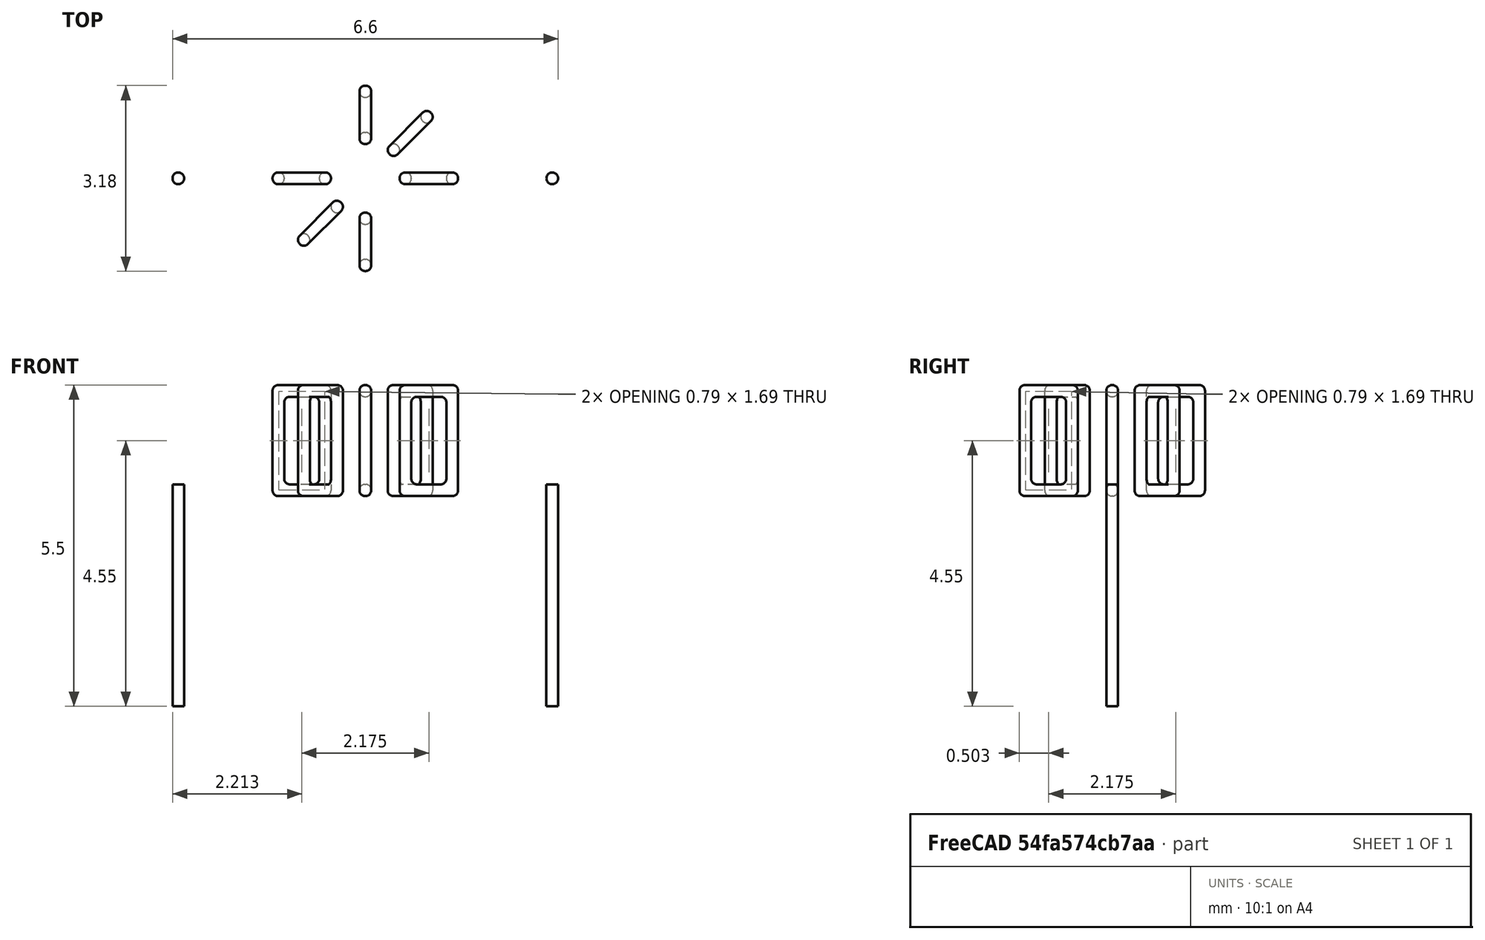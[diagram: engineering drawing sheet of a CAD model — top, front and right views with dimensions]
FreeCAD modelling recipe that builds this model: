
FCSTD DOCUMENT  (FreeCAD 0.16R6703 (Git))
Label: L_Toroid_Horizontal_D3.2mm_P6.40mm_Diameter3-5mm_Amidon-T12
License: All rights reserved
LicenseURL: http://en.wikipedia.org/wiki/All_rights_reserved
objects: Sketcher::SketchObject×6, PartDesign::Pad×6, PartDesign::Fillet×5, Spreadsheet::Sheet×1
note: 23 computed .brp shape members not serialized (recipe doc carries the construction recipe); baked Part::Feature solids carry a one-line shape summary decoded from their .brp

FEATURE [Spreadsheet::Sheet] Spreadsheet  label="dimensions"
  cells = A1=Wx; B1(Wx)=3.175; C1(WW)=1.5748; D1=3.175; A2=Wy; B2(Wy)=3.175; D2=3.175; A3=RM; B3(RMx)=6.4; C3(RMy)=0; A4=d_wire; B4(d_wire)=0.2; A5=H; B5(H)=1.5; A6=offsetx; B6(offsetx)=-1.6125
FEATURE [Sketcher::SketchObject] Sketch
  Placement = pos=(0,0,0.7) rot=(0,0,1;0rad)
  expr: Placement.Base.z = 0.5 + Spreadsheet.d_wire
  expr: Constraints[0] = Spreadsheet.Wx / 2 - Spreadsheet.d_wire
  expr: Constraints[4] = Spreadsheet.WW / 2
  expr: Constraints[2] = Spreadsheet.RMy / 2
  expr: Constraints[1] = Spreadsheet.RMx / 2
  sketch-geometry (2):
    g0: Circle CenterX=3.2 CenterY=0 CenterZ=0 NormalX=0 NormalY=0 NormalZ=1 Radius=1.3875
    g1: Circle CenterX=3.2 CenterY=0 CenterZ=0 NormalX=0 NormalY=0 NormalZ=1 Radius=0.7874
  constraints (5):
    c: Radius(g0) = 1.3875
    c: DistanceX(g-1,g0) = 3.2
    c: DistanceY(g-1,g0) = 0
    c: Coincident(g1,g0)
    c: Radius(g1) = 0.7874
FEATURE [PartDesign::Pad] Pad
  Length = 1.5
  Length2 = 100
  Placement = pos=(0,0,0.7) rot=(0,0,1;0rad)
  Sketch = -> Sketch
  Type = 0
  expr: Length = Spreadsheet.H
FEATURE [Sketcher::SketchObject] Sketch001
  Placement = pos=(0,0,0.6) rot=(0,0,1;0rad)
  expr: Placement.Base.z = 0.5 + Spreadsheet.d_wire * 0.5
  expr: Constraints[4] = Spreadsheet.RMx
  expr: Constraints[2] = Spreadsheet.RMy
  expr: Constraints[1] = Spreadsheet.d_wire / 2
  sketch-geometry (2):
    g0: Circle CenterX=0 CenterY=0 CenterZ=0 NormalX=0 NormalY=0 NormalZ=1 Radius=0.1
    g1: Circle CenterX=6.4 CenterY=0 CenterZ=0 NormalX=0 NormalY=0 NormalZ=1 Radius=0.1
  constraints (5):
    c: Equal(g0,g1)
    c: Radius(g0) = 0.1
    c: DistanceY(g-1,g1) = 0
    c: Coincident(g0,g-1)
    c: DistanceX(g-1,g1) = 6.4
FEATURE [PartDesign::Pad] Pad001
  Length = 0.1
  Length2 = 3.7
  Placement = pos=(0,0,0.6) rot=(0,0,1;0rad)
  Reversed = true
  Sketch = -> Sketch001
  Type = 4
  expr: Length2 = 3.5 + Spreadsheet.d_wire
  expr: Length = Spreadsheet.d_wire / 2
FEATURE [PartDesign::Fillet] Fillet
  Base = -> Pad [Edge6,Edge3,Edge2]
  Placement = pos=(0,0,0.7) rot=(0,0,1;0rad)
  Radius = 0.5
FEATURE [Sketcher::SketchObject] Sketch003
  Placement = pos=(3.2,0,0) rot=(1,0,0;1.5708rad)
  expr: Placement.Base.x = Spreadsheet.RMx / 2
  expr: Constraints[49] = Spreadsheet.Wx - Spreadsheet.d_wire * 2
  expr: Constraints[44] = Spreadsheet.d_wire
  expr: Constraints[23] = Spreadsheet.H
  expr: Constraints[22] = Spreadsheet.Wx / 2 - Spreadsheet.d_wire
  expr: Placement.Base.y = Spreadsheet.RMy / 2
  expr: Constraints[21] = (Spreadsheet.Wx - Spreadsheet.WW) / 2 - Spreadsheet.d_wire
  expr: Constraints[19] = Spreadsheet.d_wire
  expr: Constraints[17] = Spreadsheet.d_wire
  expr: Constraints[18] = Spreadsheet.d_wire
  expr: Constraints[16] = Spreadsheet.d_wire
  sketch-geometry (16):
    g0: LineSegment StartX=-0.5874 StartY=0.5 StartZ=0 EndX=-1.5875 EndY=0.5 EndZ=0
    g1: LineSegment StartX=-1.5875 StartY=0.5 StartZ=0 EndX=-1.5875 EndY=2.4 EndZ=0
    g2: LineSegment StartX=-1.5875 StartY=2.4 StartZ=0 EndX=-0.5874 EndY=2.4 EndZ=0
    g3: LineSegment StartX=-0.5874 StartY=2.4 StartZ=0 EndX=-0.5874 EndY=0.5 EndZ=0
    g4: LineSegment StartX=-1.3875 StartY=2.2 StartZ=0 EndX=-0.7874 EndY=2.2 EndZ=0
    g5: LineSegment StartX=-0.7874 StartY=2.2 StartZ=0 EndX=-0.7874 EndY=0.7 EndZ=0
    g6: LineSegment StartX=-0.7874 StartY=0.7 StartZ=0 EndX=-1.3875 EndY=0.7 EndZ=0
    g7: LineSegment StartX=-1.3875 StartY=0.7 StartZ=0 EndX=-1.3875 EndY=2.2 EndZ=0
    g8: LineSegment StartX=0.5874 StartY=2.4 StartZ=0 EndX=1.5875 EndY=2.4 EndZ=0
    g9: LineSegment StartX=1.5875 StartY=2.4 StartZ=0 EndX=1.5875 EndY=0.5 EndZ=0
    g10: LineSegment StartX=1.5875 StartY=0.5 StartZ=0 EndX=0.5874 EndY=0.5 EndZ=0
    g11: LineSegment StartX=0.5874 StartY=0.5 StartZ=0 EndX=0.5874 EndY=2.4 EndZ=0
    g12: LineSegment StartX=0.7874 StartY=2.2 StartZ=0 EndX=1.3875 EndY=2.2 EndZ=0
    g13: LineSegment StartX=1.3875 StartY=2.2 StartZ=0 EndX=1.3875 EndY=0.7 EndZ=0
    g14: LineSegment StartX=1.3875 StartY=0.7 StartZ=0 EndX=0.7874 EndY=0.7 EndZ=0
    g15: LineSegment StartX=0.7874 StartY=0.7 StartZ=0 EndX=0.7874 EndY=2.2 EndZ=0
  constraints (50):
    c: Horizontal(g0)
    c: Coincident(g1,g0)
    c: Vertical(g1)
    c: Coincident(g2,g1)
    c: Horizontal(g2)
    c: Coincident(g3,g2)
    c: Coincident(g3,g0)
    c: Vertical(g3)
    c: Coincident(g4,g5)
    c: Coincident(g5,g6)
    c: Coincident(g6,g7)
    c: Coincident(g7,g4)
    c: Horizontal(g4)
    c: Horizontal(g6)
    c: Vertical(g5)
    c: Vertical(g7)
    c: DistanceX(g1,g4) = 0.2
    c: DistanceY(g4,g1) = 0.2
    c: DistanceX(g5,g0) = 0.2
    c: DistanceY(g0,g5) = 0.2
    c: DistanceY(g-1,g0) = 0.5
    c: DistanceX(g6,g6) = 0.6001
    c: DistanceX(g6,g-1) = 1.3875
    c: DistanceY(g7,g7) = 1.5
    c: Coincident(g8,g9)
    c: Coincident(g9,g10)
    c: Coincident(g10,g11)
    c: Coincident(g11,g8)
    c: Horizontal(g8)
    c: Horizontal(g10)
    c: Vertical(g9)
    c: Vertical(g11)
    c: Coincident(g12,g13)
    c: Coincident(g13,g14)
    c: Coincident(g14,g15)
    c: Coincident(g15,g12)
    c: Horizontal(g12)
    c: Horizontal(g14)
    c: Vertical(g13)
    c: Vertical(g15)
    c: DistanceY(g8,g2) = 0
    c: DistanceY(g10,g0) = 0
    c: DistanceY(g14,g5) = 0
    c: DistanceY(g12,g4) = 0
    c: DistanceX(g8,g12) = 0.2
    c: Equal(g8,g2)
    c: Equal(g12,g4)
    c: Equal(g9,g1)
    c: Equal(g13,g7)
    c: DistanceX(g4,g12) = 2.775
FEATURE [PartDesign::Pad] Pad002
  Length = 0.2
  Length2 = 100
  Midplane = true
  Placement = pos=(3.2,0,0) rot=(1,0,0;1.5708rad)
  Sketch = -> Sketch003
  Type = 0
  expr: Length = Spreadsheet.d_wire
FEATURE [PartDesign::Fillet] Fillet001
  Base = -> Pad002 [Edge38,Edge41,Edge42,Edge43,Edge29,Edge32,Edge33,Edge34,Edge25,Edge35,Edge36,Edge13,Edge14,Edge15,Edge16,Edge17,Edge18,Edge19,Edge1,Edge2,Edge3,Edge4,Edge5,Edge6,Edge7,Edge37,Edge39,Edge40,Edge20,Edge23,Edge24,Edge21,Edge22,Edge8,Edge9,Edge10,Edge11,Edge12,Edge26,Edge27,+8 more]
  Placement = pos=(3.2,0,0) rot=(1,0,0;1.5708rad)
  Radius = 0.094
  expr: Radius = Spreadsheet.d_wire * 0.47
FEATURE [Sketcher::SketchObject] Sketch004
  Placement = pos=(3.2,0,0) rot=(0.862856,0.357407,0.357407;1.71777rad)
  expr: Placement.Base.x = Spreadsheet.RMx / 2
  expr: Constraints[49] = Spreadsheet.Wx - 2 * Spreadsheet.d_wire
  expr: Constraints[44] = Spreadsheet.d_wire
  expr: Constraints[23] = Spreadsheet.H
  expr: Constraints[22] = Spreadsheet.Wx / 2 - Spreadsheet.d_wire
  expr: Placement.Base.y = Spreadsheet.RMy / 2
  expr: Constraints[21] = (Spreadsheet.Wx - Spreadsheet.WW) / 2 - Spreadsheet.d_wire
  expr: Constraints[19] = Spreadsheet.d_wire
  expr: Constraints[17] = Spreadsheet.d_wire
  expr: Constraints[18] = Spreadsheet.d_wire
  expr: Constraints[16] = Spreadsheet.d_wire
  sketch-geometry (16):
    g0: LineSegment StartX=-0.5874 StartY=0.5 StartZ=0 EndX=-1.5875 EndY=0.5 EndZ=0
    g1: LineSegment StartX=-1.5875 StartY=0.5 StartZ=0 EndX=-1.5875 EndY=2.4 EndZ=0
    g2: LineSegment StartX=-1.5875 StartY=2.4 StartZ=0 EndX=-0.5874 EndY=2.4 EndZ=0
    g3: LineSegment StartX=-0.5874 StartY=2.4 StartZ=0 EndX=-0.5874 EndY=0.5 EndZ=0
    g4: LineSegment StartX=-1.3875 StartY=2.2 StartZ=0 EndX=-0.7874 EndY=2.2 EndZ=0
    g5: LineSegment StartX=-0.7874 StartY=2.2 StartZ=0 EndX=-0.7874 EndY=0.7 EndZ=0
    g6: LineSegment StartX=-0.7874 StartY=0.7 StartZ=0 EndX=-1.3875 EndY=0.7 EndZ=0
    g7: LineSegment StartX=-1.3875 StartY=0.7 StartZ=0 EndX=-1.3875 EndY=2.2 EndZ=0
    g8: LineSegment StartX=0.5874 StartY=2.4 StartZ=0 EndX=1.5875 EndY=2.4 EndZ=0
    g9: LineSegment StartX=1.5875 StartY=2.4 StartZ=0 EndX=1.5875 EndY=0.5 EndZ=0
    g10: LineSegment StartX=1.5875 StartY=0.5 StartZ=0 EndX=0.5874 EndY=0.5 EndZ=0
    g11: LineSegment StartX=0.5874 StartY=0.5 StartZ=0 EndX=0.5874 EndY=2.4 EndZ=0
    g12: LineSegment StartX=0.7874 StartY=2.2 StartZ=0 EndX=1.3875 EndY=2.2 EndZ=0
    g13: LineSegment StartX=1.3875 StartY=2.2 StartZ=0 EndX=1.3875 EndY=0.7 EndZ=0
    g14: LineSegment StartX=1.3875 StartY=0.7 StartZ=0 EndX=0.7874 EndY=0.7 EndZ=0
    g15: LineSegment StartX=0.7874 StartY=0.7 StartZ=0 EndX=0.7874 EndY=2.2 EndZ=0
  constraints (50):
    c: Horizontal(g0)
    c: Coincident(g1,g0)
    c: Vertical(g1)
    c: Coincident(g2,g1)
    c: Horizontal(g2)
    c: Coincident(g3,g2)
    c: Coincident(g3,g0)
    c: Vertical(g3)
    c: Coincident(g4,g5)
    c: Coincident(g5,g6)
    c: Coincident(g6,g7)
    c: Coincident(g7,g4)
    c: Horizontal(g4)
    c: Horizontal(g6)
    c: Vertical(g5)
    c: Vertical(g7)
    c: DistanceX(g1,g4) = 0.2
    c: DistanceY(g4,g1) = 0.2
    c: DistanceX(g5,g0) = 0.2
    c: DistanceY(g0,g5) = 0.2
    c: DistanceY(g-1,g0) = 0.5
    c: DistanceX(g6,g6) = 0.6001
    c: DistanceX(g6,g-1) = 1.3875
    c: DistanceY(g7,g7) = 1.5
    c: Coincident(g8,g9)
    c: Coincident(g9,g10)
    c: Coincident(g10,g11)
    c: Coincident(g11,g8)
    c: Horizontal(g8)
    c: Horizontal(g10)
    c: Vertical(g9)
    c: Vertical(g11)
    c: Coincident(g12,g13)
    c: Coincident(g13,g14)
    c: Coincident(g14,g15)
    c: Coincident(g15,g12)
    c: Horizontal(g12)
    c: Horizontal(g14)
    c: Vertical(g13)
    c: Vertical(g15)
    c: DistanceY(g8,g2) = 0
    c: DistanceY(g10,g0) = 0
    c: DistanceY(g14,g5) = 0
    c: DistanceY(g12,g4) = 0
    c: DistanceX(g8,g12) = 0.2
    c: Equal(g8,g2)
    c: Equal(g12,g4)
    c: Equal(g9,g1)
    c: Equal(g13,g7)
    c: DistanceX(g4,g12) = 2.775
FEATURE [PartDesign::Pad] Pad003
  Length = 0.2
  Length2 = 100
  Midplane = true
  Placement = pos=(3.2,0,0) rot=(0.862856,0.357407,0.357407;1.71777rad)
  Sketch = -> Sketch004
  Type = 0
  expr: Length = Spreadsheet.d_wire
FEATURE [PartDesign::Fillet] Fillet002
  Base = -> Pad003 [Edge38,Edge41,Edge42,Edge43,Edge29,Edge32,Edge33,Edge34,Edge25,Edge35,Edge36,Edge13,Edge14,Edge15,Edge16,Edge17,Edge18,Edge19,Edge1,Edge2,Edge3,Edge4,Edge5,Edge6,Edge7,Edge37,Edge39,Edge40,Edge20,Edge23,Edge24,Edge21,Edge22,Edge8,Edge9,Edge10,Edge11,Edge12,Edge26,Edge27,+8 more]
  Placement = pos=(3.2,0,0) rot=(0.862856,0.357407,0.357407;1.71777rad)
  Radius = 0.094
  expr: Radius = Spreadsheet.d_wire * 0.47
FEATURE [Sketcher::SketchObject] Sketch005
  Placement = pos=(3.2,0,0) rot=(0.862856,-0.357407,-0.357407;1.71777rad)
  expr: Placement.Base.x = Spreadsheet.RMx / 2
  expr: Constraints[49] = Spreadsheet.Wx - 2 * Spreadsheet.d_wire
  expr: Constraints[44] = Spreadsheet.d_wire
  expr: Constraints[23] = Spreadsheet.H
  expr: Constraints[22] = Spreadsheet.Wx / 2 - Spreadsheet.d_wire
  expr: Placement.Base.y = Spreadsheet.RMy / 2
  expr: Constraints[21] = (Spreadsheet.Wx - Spreadsheet.WW) / 2 - Spreadsheet.d_wire
  expr: Constraints[19] = Spreadsheet.d_wire
  expr: Constraints[17] = Spreadsheet.d_wire
  expr: Constraints[18] = Spreadsheet.d_wire
  expr: Constraints[16] = Spreadsheet.d_wire
  sketch-geometry (16):
    g0: LineSegment StartX=-0.5874 StartY=0.5 StartZ=0 EndX=-1.5875 EndY=0.5 EndZ=0
    g1: LineSegment StartX=-1.5875 StartY=0.5 StartZ=0 EndX=-1.5875 EndY=2.4 EndZ=0
    g2: LineSegment StartX=-1.5875 StartY=2.4 StartZ=0 EndX=-0.5874 EndY=2.4 EndZ=0
    g3: LineSegment StartX=-0.5874 StartY=2.4 StartZ=0 EndX=-0.5874 EndY=0.5 EndZ=0
    g4: LineSegment StartX=-1.3875 StartY=2.2 StartZ=0 EndX=-0.7874 EndY=2.2 EndZ=0
    g5: LineSegment StartX=-0.7874 StartY=2.2 StartZ=0 EndX=-0.7874 EndY=0.7 EndZ=0
    g6: LineSegment StartX=-0.7874 StartY=0.7 StartZ=0 EndX=-1.3875 EndY=0.7 EndZ=0
    g7: LineSegment StartX=-1.3875 StartY=0.7 StartZ=0 EndX=-1.3875 EndY=2.2 EndZ=0
    g8: LineSegment StartX=0.5874 StartY=2.4 StartZ=0 EndX=1.5875 EndY=2.4 EndZ=0
    g9: LineSegment StartX=1.5875 StartY=2.4 StartZ=0 EndX=1.5875 EndY=0.5 EndZ=0
    g10: LineSegment StartX=1.5875 StartY=0.5 StartZ=0 EndX=0.5874 EndY=0.5 EndZ=0
    g11: LineSegment StartX=0.5874 StartY=0.5 StartZ=0 EndX=0.5874 EndY=2.4 EndZ=0
    g12: LineSegment StartX=0.7874 StartY=2.2 StartZ=0 EndX=1.3875 EndY=2.2 EndZ=0
    g13: LineSegment StartX=1.3875 StartY=2.2 StartZ=0 EndX=1.3875 EndY=0.7 EndZ=0
    g14: LineSegment StartX=1.3875 StartY=0.7 StartZ=0 EndX=0.7874 EndY=0.7 EndZ=0
    g15: LineSegment StartX=0.7874 StartY=0.7 StartZ=0 EndX=0.7874 EndY=2.2 EndZ=0
  constraints (50):
    c: Horizontal(g0)
    c: Coincident(g1,g0)
    c: Vertical(g1)
    c: Coincident(g2,g1)
    c: Horizontal(g2)
    c: Coincident(g3,g2)
    c: Coincident(g3,g0)
    c: Vertical(g3)
    c: Coincident(g4,g5)
    c: Coincident(g5,g6)
    c: Coincident(g6,g7)
    c: Coincident(g7,g4)
    c: Horizontal(g4)
    c: Horizontal(g6)
    c: Vertical(g5)
    c: Vertical(g7)
    c: DistanceX(g1,g4) = 0.2
    c: DistanceY(g4,g1) = 0.2
    c: DistanceX(g5,g0) = 0.2
    c: DistanceY(g0,g5) = 0.2
    c: DistanceY(g-1,g0) = 0.5
    c: DistanceX(g6,g6) = 0.6001
    c: DistanceX(g6,g-1) = 1.3875
    c: DistanceY(g7,g7) = 1.5
    c: Coincident(g8,g9)
    c: Coincident(g9,g10)
    c: Coincident(g10,g11)
    c: Coincident(g11,g8)
    c: Horizontal(g8)
    c: Horizontal(g10)
    c: Vertical(g9)
    c: Vertical(g11)
    c: Coincident(g12,g13)
    c: Coincident(g13,g14)
    c: Coincident(g14,g15)
    c: Coincident(g15,g12)
    c: Horizontal(g12)
    c: Horizontal(g14)
    c: Vertical(g13)
    c: Vertical(g15)
    c: DistanceY(g8,g2) = 0
    c: DistanceY(g10,g0) = 0
    c: DistanceY(g14,g5) = 0
    c: DistanceY(g12,g4) = 0
    c: DistanceX(g8,g12) = 0.2
    c: Equal(g8,g2)
    c: Equal(g12,g4)
    c: Equal(g9,g1)
    c: Equal(g13,g7)
    c: DistanceX(g4,g12) = 2.775
FEATURE [PartDesign::Pad] Pad004
  Length = 0.2
  Length2 = 100
  Midplane = true
  Placement = pos=(3.2,0,0) rot=(0.862856,-0.357407,-0.357407;1.71777rad)
  Sketch = -> Sketch005
  Type = 0
  expr: Length = Spreadsheet.d_wire
FEATURE [PartDesign::Fillet] Fillet003
  Base = -> Pad004 [Edge38,Edge41,Edge42,Edge43,Edge29,Edge32,Edge33,Edge34,Edge25,Edge35,Edge36,Edge13,Edge14,Edge15,Edge16,Edge17,Edge18,Edge19,Edge1,Edge2,Edge3,Edge4,Edge5,Edge6,Edge7,Edge37,Edge39,Edge40,Edge20,Edge23,Edge24,Edge21,Edge22,Edge8,Edge9,Edge10,Edge11,Edge12,Edge26,Edge27,+8 more]
  Placement = pos=(3.2,0,0) rot=(0.862856,-0.357407,-0.357407;1.71777rad)
  Radius = 0.094
  expr: Radius = Spreadsheet.d_wire * 0.47
FEATURE [Sketcher::SketchObject] Sketch006
  Placement = pos=(3.2,0,0) rot=(0.57735,0.57735,0.57735;2.0944rad)
  expr: Placement.Base.x = Spreadsheet.RMx / 2
  expr: Constraints[49] = Spreadsheet.Wx - Spreadsheet.d_wire * 2
  expr: Constraints[44] = Spreadsheet.d_wire
  expr: Constraints[23] = Spreadsheet.H
  expr: Constraints[22] = Spreadsheet.Wx / 2 - Spreadsheet.d_wire
  expr: Placement.Base.y = Spreadsheet.RMy / 2
  expr: Constraints[21] = (Spreadsheet.Wx - Spreadsheet.WW) / 2 - Spreadsheet.d_wire
  expr: Constraints[19] = Spreadsheet.d_wire
  expr: Constraints[17] = Spreadsheet.d_wire
  expr: Constraints[18] = Spreadsheet.d_wire
  expr: Constraints[16] = Spreadsheet.d_wire
  sketch-geometry (16):
    g0: LineSegment StartX=-0.5874 StartY=0.5 StartZ=0 EndX=-1.5875 EndY=0.5 EndZ=0
    g1: LineSegment StartX=-1.5875 StartY=0.5 StartZ=0 EndX=-1.5875 EndY=2.4 EndZ=0
    g2: LineSegment StartX=-1.5875 StartY=2.4 StartZ=0 EndX=-0.5874 EndY=2.4 EndZ=0
    g3: LineSegment StartX=-0.5874 StartY=2.4 StartZ=0 EndX=-0.5874 EndY=0.5 EndZ=0
    g4: LineSegment StartX=-1.3875 StartY=2.2 StartZ=0 EndX=-0.7874 EndY=2.2 EndZ=0
    g5: LineSegment StartX=-0.7874 StartY=2.2 StartZ=0 EndX=-0.7874 EndY=0.7 EndZ=0
    g6: LineSegment StartX=-0.7874 StartY=0.7 StartZ=0 EndX=-1.3875 EndY=0.7 EndZ=0
    g7: LineSegment StartX=-1.3875 StartY=0.7 StartZ=0 EndX=-1.3875 EndY=2.2 EndZ=0
    g8: LineSegment StartX=0.5874 StartY=2.4 StartZ=0 EndX=1.5875 EndY=2.4 EndZ=0
    g9: LineSegment StartX=1.5875 StartY=2.4 StartZ=0 EndX=1.5875 EndY=0.5 EndZ=0
    g10: LineSegment StartX=1.5875 StartY=0.5 StartZ=0 EndX=0.5874 EndY=0.5 EndZ=0
    g11: LineSegment StartX=0.5874 StartY=0.5 StartZ=0 EndX=0.5874 EndY=2.4 EndZ=0
    g12: LineSegment StartX=0.7874 StartY=2.2 StartZ=0 EndX=1.3875 EndY=2.2 EndZ=0
    g13: LineSegment StartX=1.3875 StartY=2.2 StartZ=0 EndX=1.3875 EndY=0.7 EndZ=0
    g14: LineSegment StartX=1.3875 StartY=0.7 StartZ=0 EndX=0.7874 EndY=0.7 EndZ=0
    g15: LineSegment StartX=0.7874 StartY=0.7 StartZ=0 EndX=0.7874 EndY=2.2 EndZ=0
  constraints (50):
    c: Horizontal(g0)
    c: Coincident(g1,g0)
    c: Vertical(g1)
    c: Coincident(g2,g1)
    c: Horizontal(g2)
    c: Coincident(g3,g2)
    c: Coincident(g3,g0)
    c: Vertical(g3)
    c: Coincident(g4,g5)
    c: Coincident(g5,g6)
    c: Coincident(g6,g7)
    c: Coincident(g7,g4)
    c: Horizontal(g4)
    c: Horizontal(g6)
    c: Vertical(g5)
    c: Vertical(g7)
    c: DistanceX(g1,g4) = 0.2
    c: DistanceY(g4,g1) = 0.2
    c: DistanceX(g5,g0) = 0.2
    c: DistanceY(g0,g5) = 0.2
    c: DistanceY(g-1,g0) = 0.5
    c: DistanceX(g6,g6) = 0.6001
    c: DistanceX(g6,g-1) = 1.3875
    c: DistanceY(g7,g7) = 1.5
    c: Coincident(g8,g9)
    c: Coincident(g9,g10)
    c: Coincident(g10,g11)
    c: Coincident(g11,g8)
    c: Horizontal(g8)
    c: Horizontal(g10)
    c: Vertical(g9)
    c: Vertical(g11)
    c: Coincident(g12,g13)
    c: Coincident(g13,g14)
    c: Coincident(g14,g15)
    c: Coincident(g15,g12)
    c: Horizontal(g12)
    c: Horizontal(g14)
    c: Vertical(g13)
    c: Vertical(g15)
    c: DistanceY(g8,g2) = 0
    c: DistanceY(g10,g0) = 0
    c: DistanceY(g14,g5) = 0
    c: DistanceY(g12,g4) = 0
    c: DistanceX(g8,g12) = 0.2
    c: Equal(g8,g2)
    c: Equal(g12,g4)
    c: Equal(g9,g1)
    c: Equal(g13,g7)
    c: DistanceX(g4,g12) = 2.775
FEATURE [PartDesign::Pad] Pad005
  Length = 0.2
  Length2 = 100
  Midplane = true
  Placement = pos=(3.2,0,0) rot=(0.57735,0.57735,0.57735;2.0944rad)
  Sketch = -> Sketch006
  Type = 0
  expr: Length = Spreadsheet.d_wire
FEATURE [PartDesign::Fillet] Fillet004
  Base = -> Pad005 [Edge38,Edge41,Edge42,Edge43,Edge29,Edge32,Edge33,Edge34,Edge25,Edge35,Edge36,Edge13,Edge14,Edge15,Edge16,Edge17,Edge18,Edge19,Edge1,Edge2,Edge3,Edge4,Edge5,Edge6,Edge7,Edge37,Edge39,Edge40,Edge20,Edge23,Edge24,Edge21,Edge22,Edge8,Edge9,Edge10,Edge11,Edge12,Edge26,Edge27,+8 more]
  Placement = pos=(3.2,0,0) rot=(0.57735,0.57735,0.57735;2.0944rad)
  Radius = 0.094
  expr: Radius = Spreadsheet.d_wire * 0.47
